# Revit family: Skylight_Fakro_DEF
name_source: partatom
category: Generic Models
units: mm (PartAtom-declared; Revit-internal decimal feet)

## family parameters
Always vertical = No
Can host rebar = No
Cut with Voids When Loaded = No
Host = Roof
Maintain Annotation Orientation = No
Part Type = Normal
Room Calculation Point = No
Round Connector Dimension = Use Diameter
Shared = No

## types (11) — shared parameters
Frame Material = Plastic - PVC - FAKRO - Insulated
Glazing = Glazing - Insulated - FAKRO - Triple Glazed
Handle Material = Metal - Steel - FAKRO
Sash Material = Metal - Steel - FAKRO - Insulated
zero-valued in all types: Default Elevation

## per-type parameters (varying)
| type | A | B | L | S |
| S82-L82-A65-B65 | 65 cm | 65 cm | 82 cm | 82 cm |
| S82-L112-A65-B95 | 65 cm | 95 cm | 112 cm | 82 cm |
| S92-L92-A75-B75 | 75 cm | 75 cm | 92 cm | 92 cm |
| S102-L102-A85-B85 | 85 cm | 85 cm | 102 cm | 102 cm |
| S112-L112-A95-B95 | 95 cm | 95 cm | 112 cm | 112 cm |
| S112-L142-A95-B125 | 95 cm | 125 cm | 142 cm | 112 cm |
| S122-L122-A105-B105 | 105 cm | 105 cm | 122 cm | 122 cm |
| S142-L142-A125-B125 | 125 cm | 125 cm | 142 cm | 142 cm |
| S162-L162-A145-B145 | 145 cm | 145 cm | 162 cm | 162 cm |
| S122-L172-A105-B155 | 105 cm | 155 cm | 172 cm | 122 cm |
| S142-L242-A125-B225 | 125 cm | 225 cm | 242 cm | 142 cm |

## geometry (parser evidence)
native form markers: Sweep x3
no freeform markers — native parametric forms only
